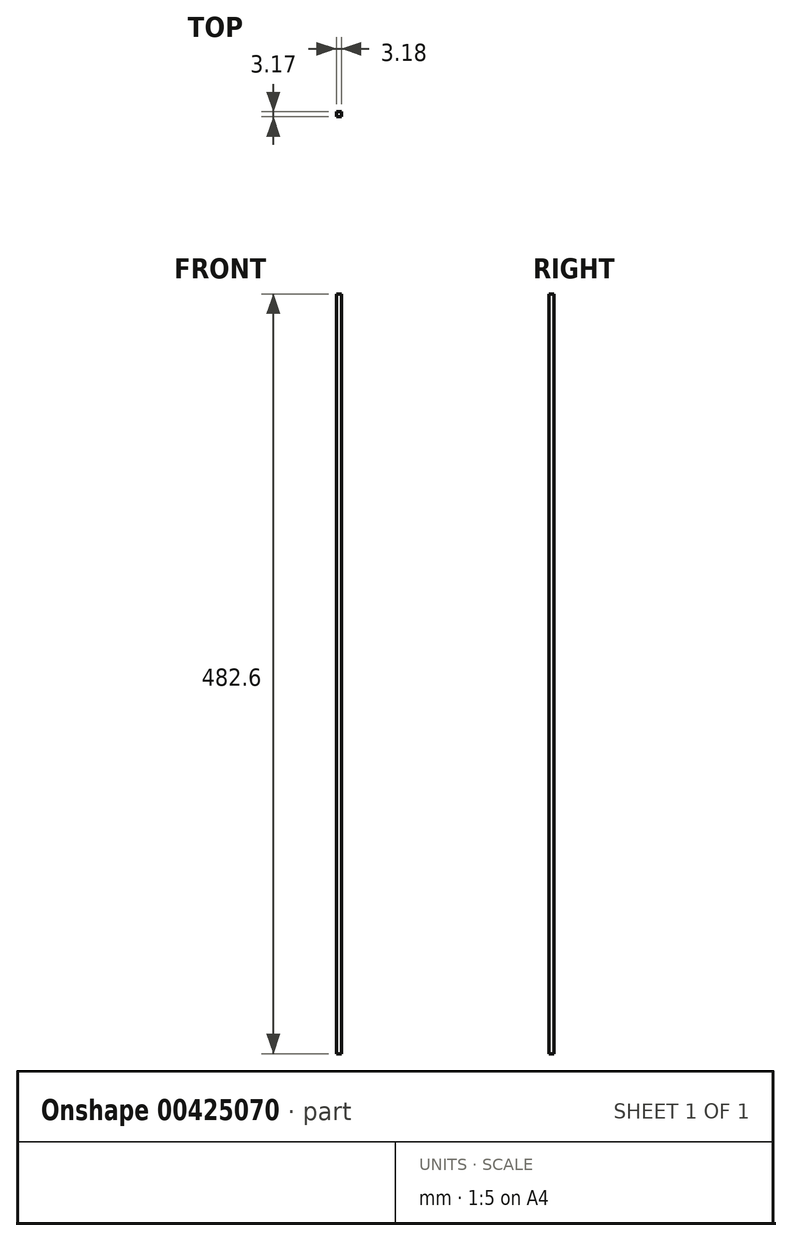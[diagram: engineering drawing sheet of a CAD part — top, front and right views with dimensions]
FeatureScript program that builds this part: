
annotation { "Feature Type Name" : "Feature", "Feature Type Description" : "" }
export const myFeature = defineFeature(function(context is Context, id is Id, definition is map)
    precondition{}
    {
        {
            var Q0;
            Q0=qCreatedBy(makeId("Front.planeOp"),FACE);
            var sketch = newSketch(context, id + "F0", { "sketchPlane" : qUnion([Q0])});
            skLineSegment(sketch, "E0", {"start": v(-109, 261.35) * mm, "end": v(-109, -221.25) * mm});
            skLineSegment(sketch, "E1", {"start": v(-109, -221.25) * mm, "end": v(-105.83, -221.25) * mm});
            skLineSegment(sketch, "E2", {"start": v(-105.83, -221.25) * mm, "end": v(-105.83, 261.35) * mm});
            skLineSegment(sketch, "E3", {"start": v(-105.83, 261.35) * mm, "end": v(-109, 261.35) * mm});
            skSolve(sketch);
        }
        {
            var Q0;
            Q0=makeQuery(id+"F0.imprint","IMPRINT",FACE,{"disambiguationData":[TD([[makeQuery(id+"F0.imprint","IMPRINT",EDGE,{"derivedFrom":sQuery(id+"F0.wireOp",EDGE,"E0")}),1.0]])]});
            extrude(context, id + "F1", {"entities" : qUnion([Q0]), "depth" : 3.17 * mm, "offsetDistance" : 25.4 * mm});
        }
    });
